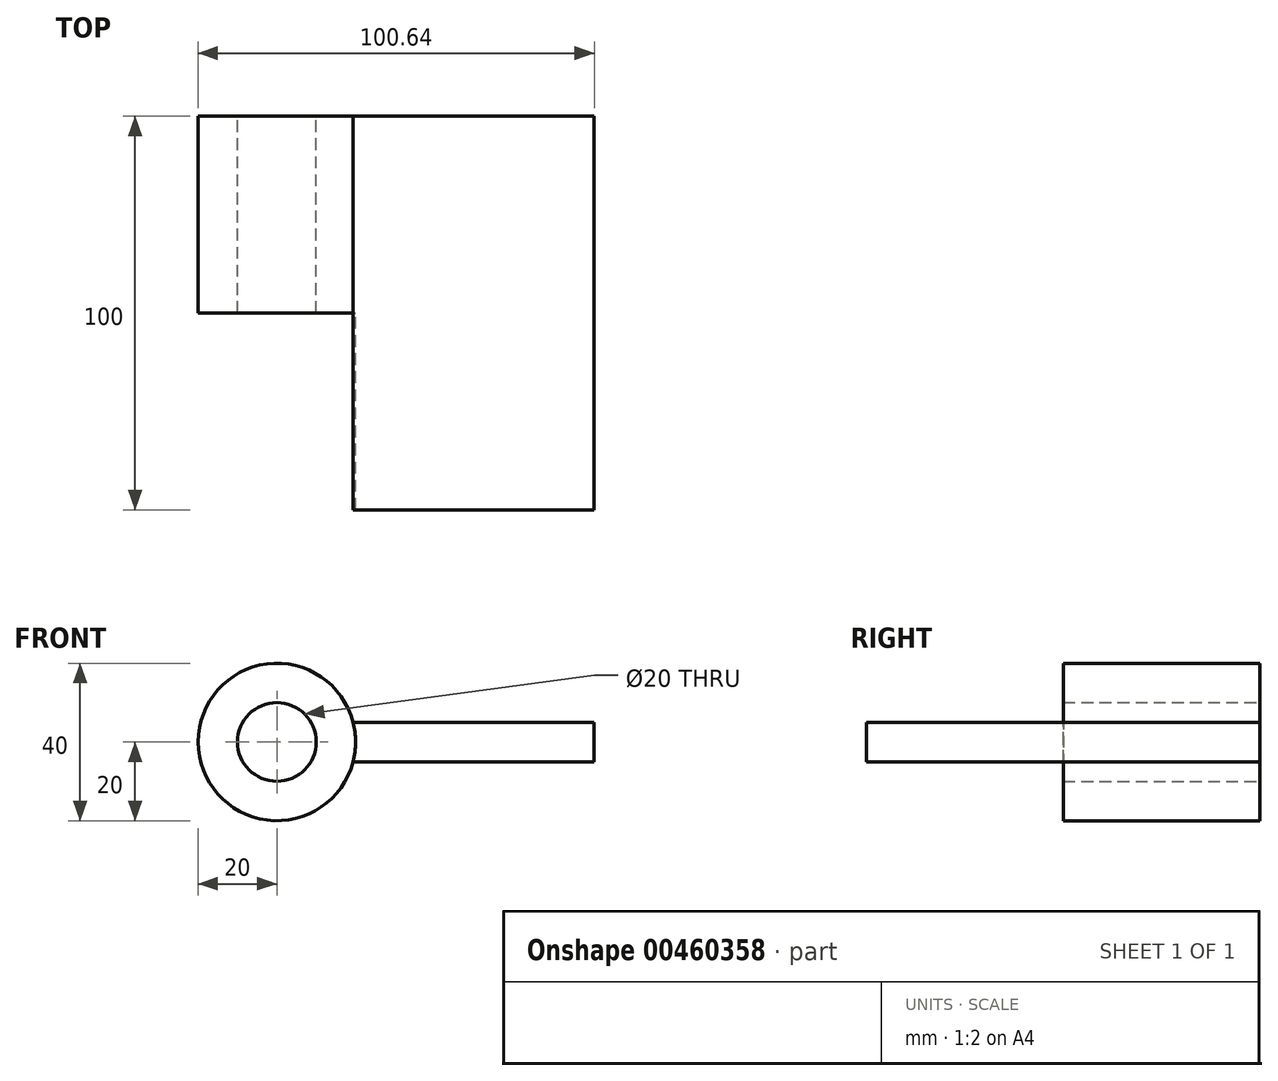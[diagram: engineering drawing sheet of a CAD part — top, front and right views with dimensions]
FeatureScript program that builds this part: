
annotation { "Feature Type Name" : "Feature", "Feature Type Description" : "" }
export const myFeature = defineFeature(function(context is Context, id is Id, definition is map)
    precondition{}
    {
        {
            var Q0;
            Q0=qCreatedBy(makeId("Front.planeOp"),FACE);
            var sketch = newSketch(context, id + "F0", { "sketchPlane" : qUnion([Q0])});
            skCircle(sketch, "E0", {"center": v(0, 0) * mm, "radius": 20 * mm});
            skCircle(sketch, "E1", {"center": v(0, 0) * mm, "radius": 10 * mm});
            skLineSegment(sketch, "E2", {"start": v(0, 0) * mm, "end": v(50, 0) * mm, "construction": true});
            skLineSegment(sketch, "E3.bottom", {"start": v(19.36, -5) * mm, "end": v(80.64, -5) * mm});
            skLineSegment(sketch, "E3.top", {"start": v(19.36, 5) * mm, "end": v(80.64, 5) * mm});
            skLineSegment(sketch, "E3.right", {"start": v(80.64, -5) * mm, "end": v(80.64, 5) * mm});
            skPoint(sketch, "E3.middle", {"position": v(50, 0) * mm});
            skSolve(sketch);
        }
        {
            var Q0;
            Q0=makeQuery(id+"F0.imprint","IMPRINT",FACE,{"disambiguationData":[TD([[makeQuery(id+"F0.imprint","IMPRINT",EDGE,{"derivedFrom":sQuery(id+"F0.wireOp",EDGE,"E1")}),-1.0]])]});
            extrude(context, id + "F1", {"entities" : qUnion([Q0]), "depth" : 50 * mm});
        }
        {
            var Q0;
            {var subQ0=sQuery(id+"F0.wireOp",EDGE,"E3.bottom");Q0=makeQuery(id+"F0.imprint","IMPRINT",FACE,{"disambiguationData":[TD([[makeQuery(id+"F0.imprint","IMPRINT",EDGE,{"derivedFrom":subQ0}),1.0]])]});}
            extrude(context, id + "F2", {"entities" : qUnion([Q0]), "operationType" : NewBodyOperationType.ADD, "depth" : 100 * mm});
        }
    });
